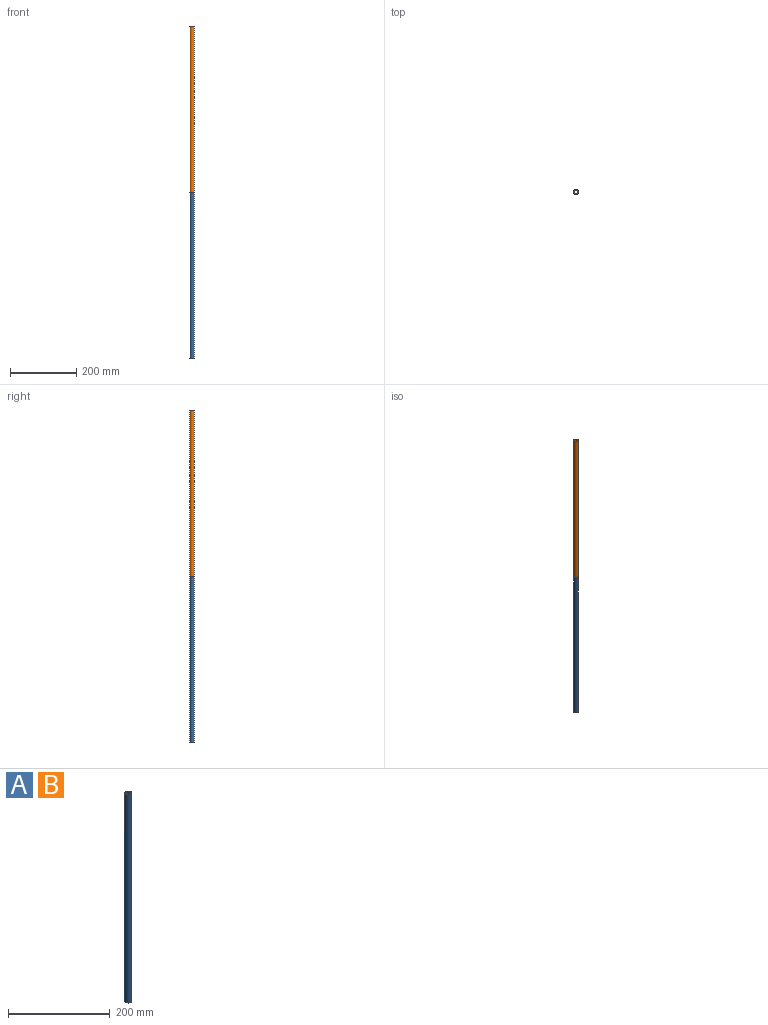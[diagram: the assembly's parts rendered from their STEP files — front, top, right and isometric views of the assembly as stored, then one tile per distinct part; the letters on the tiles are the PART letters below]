
ASSEMBLY  parts=2 mates=1
PART A: 4 faces, bbox 14x14x500 mm
  f0: cylinder r=5mm len=500mm, axis (0,0,-1), area 15708mm2, adj f2,f3
  f1: cylinder r=7mm len=500mm, axis (0,0,-1), area 21991.1mm2, adj f2,f3
  f2: plane 14x14mm, normal (0,0,1), area 75.4mm2, adj f0,f1
  f3: plane 14x14mm, normal (0,0,-1), area 75.4mm2, adj f0,f1
PART B: same geometry as A
PLACE A t=(-38.15,-8.12,-229.14)mm
PLACE B rot(axis=(1,0,0),180deg) t=(-38.15,-8.12,770.86)mm
MATE fastened B.f0 <-> A.f1  axis (0,0,-1) through (-38.15,-8.12,270.86)mm
